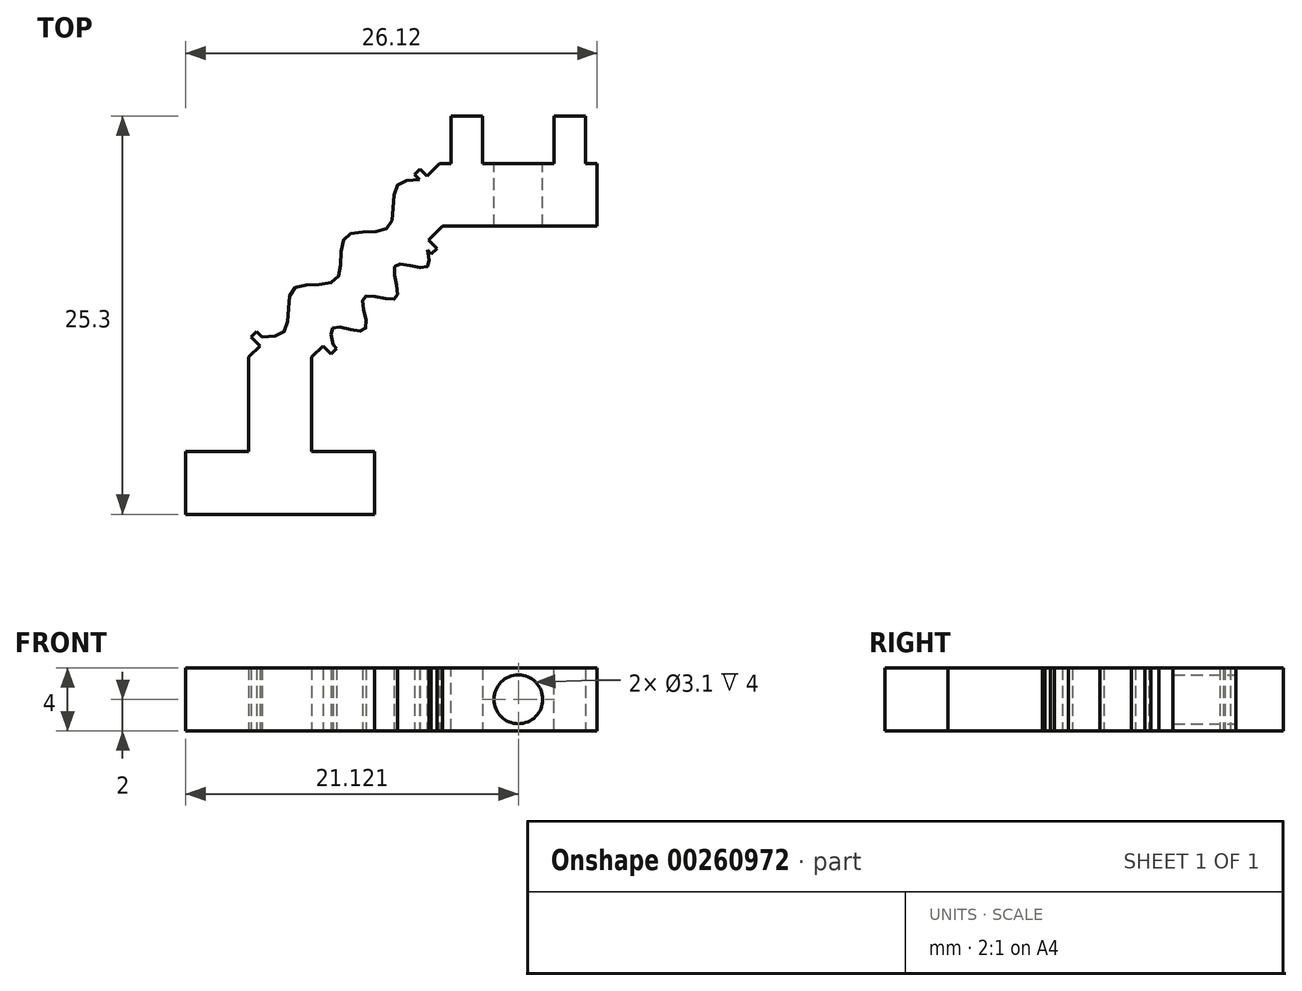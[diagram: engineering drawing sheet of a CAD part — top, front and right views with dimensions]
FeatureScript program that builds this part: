
annotation { "Feature Type Name" : "Feature", "Feature Type Description" : "" }
export const myFeature = defineFeature(function(context is Context, id is Id, definition is map)
    precondition{}
    {
        {
            var Q0;
            Q0=qCreatedBy(makeId("Top.planeOp"),FACE);
            var sketch = newSketch(context, id + "F0", { "sketchPlane" : qUnion([Q0])});
            skLineSegment(sketch, "E0", {"start": v(8, 0) * mm, "end": v(4, 0) * mm});
            skLineSegment(sketch, "E1", {"start": v(4, 4) * mm, "end": v(4, 10) * mm});
            skLineSegment(sketch, "E2", {"start": v(8, 4) * mm, "end": v(12, 4) * mm});
            skLineSegment(sketch, "E3", {"start": v(12, 4) * mm, "end": v(12, 0) * mm});
            skLineSegment(sketch, "E4", {"start": v(12, 0) * mm, "end": v(8, 0) * mm});
            skLineSegment(sketch, "E5", {"start": v(4, 0) * mm, "end": v(0, 0) * mm});
            skLineSegment(sketch, "E6", {"start": v(0, 0) * mm, "end": v(0, 4) * mm});
            skLineSegment(sketch, "E7", {"start": v(0, 4) * mm, "end": v(4, 4) * mm});
            skLineSegment(sketch, "E8", {"start": v(8, 4) * mm, "end": v(8, 10) * mm});
            skLineSegment(sketch, "E9", {"start": v(5.33, 10.8) * mm, "end": v(7, 12.46) * mm, "construction": true});
            skLineSegment(sketch, "E10", {"start": v(7, 12.46) * mm, "end": v(8.66, 14.13) * mm, "construction": true});
            skLineSegment(sketch, "E11", {"start": v(8.66, 14.13) * mm, "end": v(10.33, 15.8) * mm, "construction": true});
            skLineSegment(sketch, "E12", {"start": v(10.33, 15.8) * mm, "end": v(12, 17.46) * mm, "construction": true});
            skLineSegment(sketch, "E13", {"start": v(12, 17.46) * mm, "end": v(13.66, 19.13) * mm, "construction": true});
            skLineSegment(sketch, "E14", {"start": v(13.66, 19.13) * mm, "end": v(15.33, 20.8) * mm, "construction": true});
            skLineSegment(sketch, "E15", {"start": v(6.16, 11.63) * mm, "end": v(6.69, 11.1) * mm, "construction": true});
            skLineSegment(sketch, "E16", {"start": v(7.83, 13.3) * mm, "end": v(7.3, 13.83) * mm, "construction": true});
            skLineSegment(sketch, "E17", {"start": v(9.5, 14.96) * mm, "end": v(10.02, 14.43) * mm, "construction": true});
            skLineSegment(sketch, "E18", {"start": v(11.16, 16.63) * mm, "end": v(10.63, 17.16) * mm, "construction": true});
            skLineSegment(sketch, "E19", {"start": v(12.83, 18.3) * mm, "end": v(13.36, 17.77) * mm, "construction": true});
            skLineSegment(sketch, "E20", {"start": v(14.5, 19.96) * mm, "end": v(13.96, 20.5) * mm, "construction": true});
            skLineSegment(sketch, "E21", {"start": v(8.8, 11.33) * mm, "end": v(9.8, 12.33) * mm, "construction": true});
            skLineSegment(sketch, "E22", {"start": v(9.8, 12.33) * mm, "end": v(10.8, 13.33) * mm, "construction": true});
            skLineSegment(sketch, "E23", {"start": v(10.8, 13.33) * mm, "end": v(11.8, 14.33) * mm, "construction": true});
            skLineSegment(sketch, "E24", {"start": v(11.8, 14.33) * mm, "end": v(12.8, 15.33) * mm, "construction": true});
            skLineSegment(sketch, "E25", {"start": v(12.8, 15.33) * mm, "end": v(13.8, 16.33) * mm, "construction": true});
            skLineSegment(sketch, "E26", {"start": v(13.8, 16.33) * mm, "end": v(14.8, 17.33) * mm, "construction": true});
            skLineSegment(sketch, "E27", {"start": v(9.3, 11.83) * mm, "end": v(8.77, 12.36) * mm, "construction": true});
            skLineSegment(sketch, "E28", {"start": v(10.3, 12.83) * mm, "end": v(10.83, 12.3) * mm});
            skLineSegment(sketch, "E29", {"start": v(11.3, 13.83) * mm, "end": v(10.77, 14.36) * mm, "construction": true});
            skLineSegment(sketch, "E30", {"start": v(12.3, 14.83) * mm, "end": v(12.83, 14.3) * mm, "construction": true});
            skLineSegment(sketch, "E31", {"start": v(13.3, 15.83) * mm, "end": v(12.77, 16.36) * mm, "construction": true});
            skLineSegment(sketch, "E32", {"start": v(14.3, 16.83) * mm, "end": v(14.83, 16.3) * mm, "construction": true});
            skFitSpline(sketch, "E33", {"points": [v(5.27, 10.85) * mm, v(6.64, 11.15) * mm, v(6.94, 12.52) * mm, v(7.24, 13.88) * mm, v(8.6, 14.18) * mm, v(9.97, 14.48) * mm, v(10.27, 15.85) * mm, v(10.58, 17.21) * mm, v(11.94, 17.52) * mm, v(13.3, 17.82) * mm, v(13.6, 19.18) * mm, v(13.9, 20.55) * mm, v(15.27, 20.85) * mm], "startDerivative": vector(19.55, 0.45) * mm, "endDerivative": vector(19.55, 0.45) * mm});
            skLineSegment(sketch, "E34", {"start": v(15.33, 20.8) * mm, "end": v(14.8, 21.33) * mm});
            skFitSpline(sketch, "E35", {"points": [v(8.78, 11.34) * mm, v(8.75, 12.37) * mm, v(9.78, 12.34) * mm, v(10.8, 12.31) * mm, v(10.78, 13.34) * mm, v(10.75, 14.37) * mm, v(11.78, 14.34) * mm, v(12.8, 14.31) * mm, v(12.78, 15.34) * mm, v(12.75, 16.37) * mm, v(13.78, 16.34) * mm, v(14.8, 16.31) * mm, v(14.78, 17.34) * mm], "startDerivative": vector(-3.55, 15.55) * mm, "endDerivative": vector(-3.54, 15.55) * mm});
            skFitSpline(sketch, "E36", {"points": [v(9.34, 10.78) * mm, v(9.31, 11.8) * mm, v(10.34, 11.78) * mm, v(11.37, 11.75) * mm, v(11.34, 12.78) * mm, v(11.31, 13.8) * mm, v(12.34, 13.78) * mm, v(13.37, 13.75) * mm, v(13.34, 14.78) * mm, v(13.31, 15.8) * mm, v(14.34, 15.78) * mm, v(15.37, 15.75) * mm, v(15.34, 16.78) * mm], "startDerivative": vector(-3.55, 15.55) * mm, "endDerivative": vector(-3.54, 15.55) * mm});
            skLineSegment(sketch, "E37", {"start": v(16.3, 18.3) * mm, "end": v(26.12, 18.3) * mm});
            skLineSegment(sketch, "E38", {"start": v(26.12, 18.3) * mm, "end": v(26.12, 22.3) * mm});
            skLineSegment(sketch, "E39", {"start": v(26.12, 22.3) * mm, "end": v(16.12, 22.3) * mm});
            skLineSegment(sketch, "E40", {"start": v(8, 10) * mm, "end": v(8.88, 10.88) * mm});
            skLineSegment(sketch, "E41", {"start": v(14.53, 17.6) * mm, "end": v(14.88, 17.94) * mm});
            skLineSegment(sketch, "E42", {"start": v(15.6, 16.53) * mm, "end": v(15.94, 16.88) * mm});
            skLineSegment(sketch, "E43", {"start": v(15.94, 16.88) * mm, "end": v(14.88, 17.94) * mm});
            skLineSegment(sketch, "E44", {"start": v(15.41, 17.41) * mm, "end": v(16.3, 18.3) * mm});
            skPoint(sketch, "E45.endSnap0", {"position": v(5.46, 10.66) * mm});
            skLineSegment(sketch, "E46", {"start": v(4, 10) * mm, "end": v(4.88, 10.88) * mm});
            skLineSegment(sketch, "E47", {"start": v(15.33, 20.8) * mm, "end": v(15.41, 20.7) * mm});
            skLineSegment(sketch, "E48", {"start": v(14.8, 21.33) * mm, "end": v(14.53, 21.6) * mm});
            skLineSegment(sketch, "E49", {"start": v(14.53, 21.6) * mm, "end": v(14.88, 21.94) * mm});
            skLineSegment(sketch, "E50", {"start": v(15.41, 20.7) * mm, "end": v(15.77, 21.06) * mm});
            skLineSegment(sketch, "E51", {"start": v(14.88, 21.94) * mm, "end": v(15.77, 21.06) * mm});
            skLineSegment(sketch, "E52", {"start": v(15.33, 21.5) * mm, "end": v(16.12, 22.3) * mm});
            skLineSegment(sketch, "E53", {"start": v(14.53, 17.6) * mm, "end": v(15.6, 16.53) * mm});
            skLineSegment(sketch, "E54", {"start": v(4.5, 11.63) * mm, "end": v(5.63, 10.5) * mm});
            skLineSegment(sketch, "E55", {"start": v(4.88, 10.88) * mm, "end": v(5.06, 11.06) * mm});
            skLineSegment(sketch, "E56", {"start": v(4.8, 11.33) * mm, "end": v(5.06, 11.06) * mm});
            skLineSegment(sketch, "E57", {"start": v(5.06, 11.06) * mm, "end": v(4.85, 11.27) * mm});
            skFitSpline(sketch, "E58", {"points": [v(4.85, 11.27) * mm, v(6.21, 11.58) * mm, v(6.52, 12.94) * mm, v(6.82, 14.3) * mm, v(8.18, 14.6) * mm, v(9.55, 14.9) * mm, v(9.85, 16.27) * mm, v(10.15, 17.64) * mm, v(11.52, 17.94) * mm, v(12.88, 18.24) * mm, v(13.18, 19.6) * mm, v(13.48, 20.97) * mm, v(14.85, 21.27) * mm], "startDerivative": vector(19.55, 0.45) * mm, "endDerivative": vector(19.55, 0.45) * mm});
            skLineSegment(sketch, "E59", {"start": v(5.06, 11.06) * mm, "end": v(5.27, 10.85) * mm});
            skLineSegment(sketch, "E60", {"start": v(9.06, 11.06) * mm, "end": v(8.78, 11.34) * mm});
            skLineSegment(sketch, "E61", {"start": v(9.06, 11.06) * mm, "end": v(9.34, 10.78) * mm});
            skLineSegment(sketch, "E62", {"start": v(8.53, 11.6) * mm, "end": v(9.6, 10.53) * mm});
            skLineSegment(sketch, "E63", {"start": v(8.53, 11.6) * mm, "end": v(9.06, 11.06) * mm});
            skLineSegment(sketch, "E64", {"start": v(4.5, 11.63) * mm, "end": v(4.14, 11.27) * mm});
            skLineSegment(sketch, "E65", {"start": v(5.63, 10.5) * mm, "end": v(5.27, 10.14) * mm});
            skLineSegment(sketch, "E66", {"start": v(4.14, 11.27) * mm, "end": v(5.27, 10.14) * mm});
            skLineSegment(sketch, "E67", {"start": v(9.6, 10.53) * mm, "end": v(9.24, 10.18) * mm});
            skLineSegment(sketch, "E68", {"start": v(8.53, 11.6) * mm, "end": v(8.18, 11.24) * mm});
            skLineSegment(sketch, "E69", {"start": v(8.18, 11.24) * mm, "end": v(9.24, 10.18) * mm});
            skSolve(sketch);
        }
        {
            var Q0;
            Q0=qSketchRegion(id+"F0",true);
            extrude(context, id + "F1", {"entities" : qUnion([Q0]), "depth" : 4 * mm});
        }
        {
            var Q0;
            Q0=makeQuery(id+"F1.opExtrude","SWEPT_FACE",FACE,{"disambiguationData":[OSD([sQuery(id+"F0.wireOp",EDGE,"E39")])]});
            var sketch = newSketch(context, id + "F2", { "sketchPlane" : qUnion([Q0])});
            skLineSegment(sketch, "E70", {"start": v(-26.12, 4) * mm, "end": v(-25.4, 4) * mm});
            skLineSegment(sketch, "E71", {"start": v(-25.4, 4) * mm, "end": v(-25.4, 0) * mm});
            skLineSegment(sketch, "E72", {"start": v(-25.4, 0) * mm, "end": v(-23.4, 0) * mm});
            skLineSegment(sketch, "E73", {"start": v(-23.4, 0) * mm, "end": v(-23.4, 4) * mm});
            skLineSegment(sketch, "E74", {"start": v(-25.4, 4) * mm, "end": v(-23.4, 4) * mm});
            skLineSegment(sketch, "E75", {"start": v(-18.85, 4) * mm, "end": v(-18.85, 0) * mm});
            skLineSegment(sketch, "E76", {"start": v(-18.85, 0) * mm, "end": v(-16.85, 0) * mm});
            skLineSegment(sketch, "E77", {"start": v(-16.85, 0) * mm, "end": v(-16.85, 4) * mm});
            skLineSegment(sketch, "E78", {"start": v(-16.85, 4) * mm, "end": v(-18.85, 4) * mm});
            skSolve(sketch);
        }
        {
            var Q0;
            Q0=qSketchRegion(id+"F2",true);
            extrude(context, id + "F3", {"entities" : qUnion([Q0]), "operationType" : NewBodyOperationType.ADD, "depth" : 3 * mm});
        }
        {
            var Q0;
            {var subQ16=sQuery(id+"F0.wireOp",EDGE,"E39");Q0=makeQuery(id+"F3.boolean.opBoolean","SPLIT",FACE,{"disambiguationData":[TD([makeQuery(id+"F3.opExtrude","SWEPT_FACE",FACE,{"disambiguationData":[OSD([sQuery(id+"F2.wireOp",EDGE,"E73")])]})])],"derivedFrom":makeQuery(id+"F1.opExtrude","SWEPT_FACE",FACE,{"disambiguationData":[OSD([subQ16])]})});}
            var sketch = newSketch(context, id + "F4", { "sketchPlane" : qUnion([Q0])});
            skCircle(sketch, "E79", {"center": v(-21.12, 2) * mm, "radius": 1.55 * mm});
            skSolve(sketch);
        }
        {
            var Q0;
            Q0=qSketchRegion(id+"F4",true);
            extrude(context, id + "F5", {"entities" : qUnion([Q0]), "operationType" : NewBodyOperationType.REMOVE, "oppositeDirection" : true, "depth" : 4 * mm});
        }
        {
            var Q0;
            Q0=makeQuery(id+"F1.opExtrude","SWEPT_BODY",BODY,{"disambiguationData":[OSD([sQuery(id+"F0.wireOp",EDGE,"E0"),sQuery(id+"F0.wireOp",EDGE,"E1"),sQuery(id+"F0.wireOp",EDGE,"E2"),sQuery(id+"F0.wireOp",EDGE,"E3"),sQuery(id+"F0.wireOp",EDGE,"E4"),sQuery(id+"F0.wireOp",EDGE,"E5"),sQuery(id+"F0.wireOp",EDGE,"E6"),sQuery(id+"F0.wireOp",EDGE,"E7"),sQuery(id+"F0.wireOp",EDGE,"E8"),sQuery(id+"F0.wireOp",EDGE,"E34"),sQuery(id+"F0.wireOp",EDGE,"E36"),sQuery(id+"F0.wireOp",EDGE,"E37"),sQuery(id+"F0.wireOp",EDGE,"E38"),sQuery(id+"F0.wireOp",EDGE,"E39"),sQuery(id+"F0.wireOp",EDGE,"E40"),sQuery(id+"F0.wireOp",EDGE,"E42"),sQuery(id+"F0.wireOp",EDGE,"E43"),sQuery(id+"F0.wireOp",EDGE,"E44"),sQuery(id+"F0.wireOp",EDGE,"E46"),sQuery(id+"F0.wireOp",EDGE,"E48"),sQuery(id+"F0.wireOp",EDGE,"E49"),sQuery(id+"F0.wireOp",EDGE,"E51"),sQuery(id+"F0.wireOp",EDGE,"E52"),sQuery(id+"F0.wireOp",EDGE,"E53"),sQuery(id+"F0.wireOp",EDGE,"E54"),sQuery(id+"F0.wireOp",EDGE,"E56"),sQuery(id+"F0.wireOp",EDGE,"E58"),sQuery(id+"F0.wireOp",EDGE,"E62"),sQuery(id+"F0.wireOp",EDGE,"E64"),sQuery(id+"F0.wireOp",EDGE,"E66"),sQuery(id+"F0.wireOp",EDGE,"E67"),sQuery(id+"F0.wireOp",EDGE,"E69")])]});
            transform(context, id + "F6", {"entities" : qUnion([Q0]), "transformType" : TransformType.TRANSLATION_3D, "dx" : 0 * mm, "dy" : 0 * mm, "dz" : 0 * mm, "makeCopy" : true});
        }
    });
